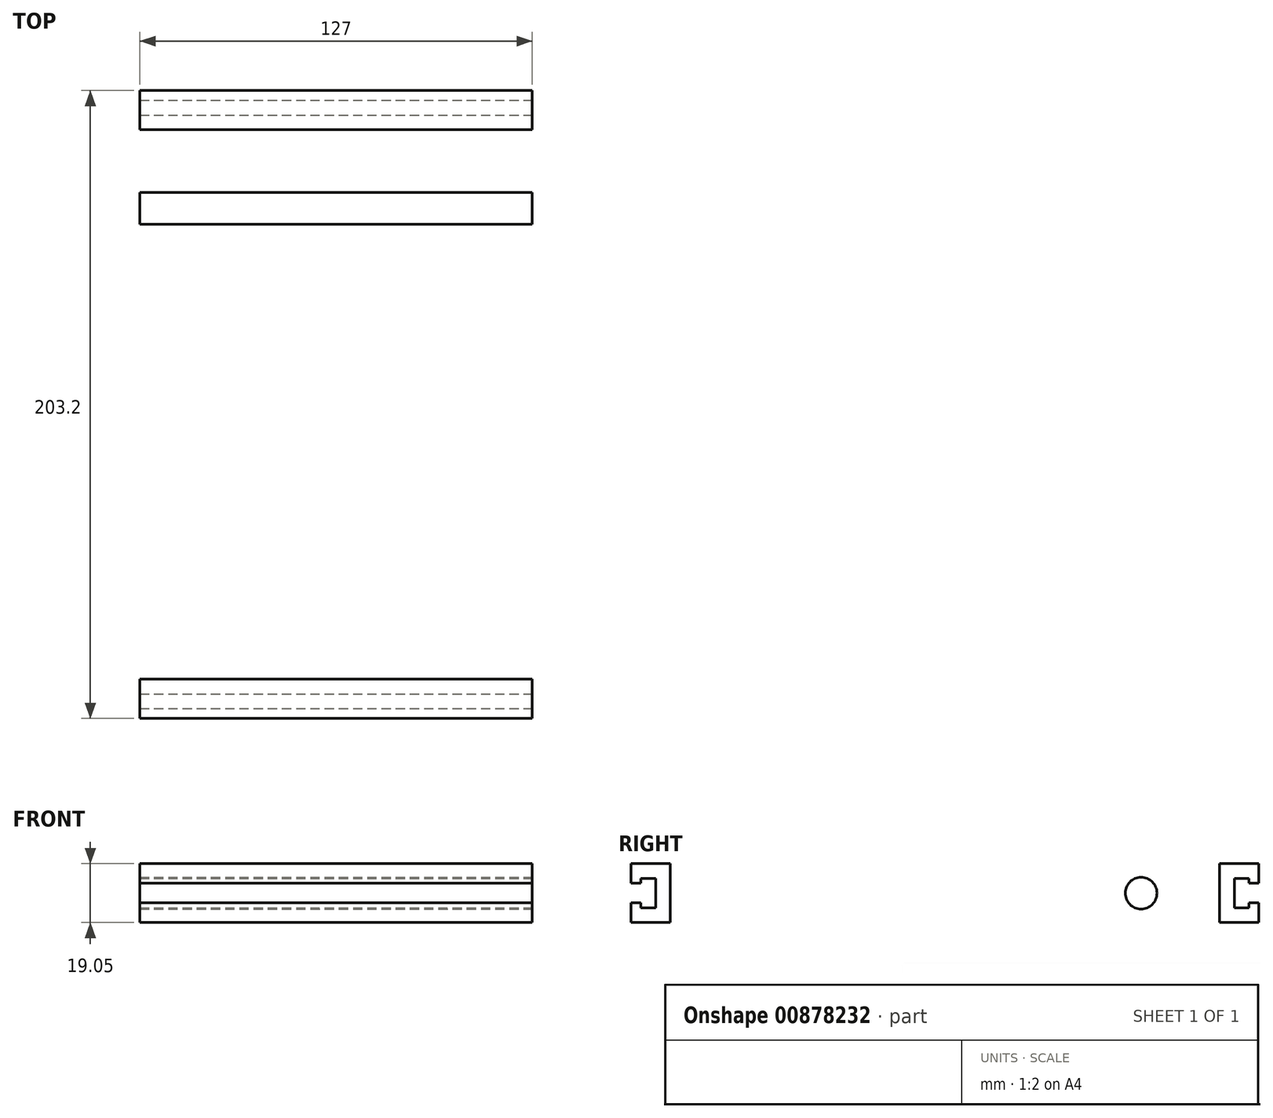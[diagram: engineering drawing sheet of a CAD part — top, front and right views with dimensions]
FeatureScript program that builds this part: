
annotation { "Feature Type Name" : "Feature", "Feature Type Description" : "" }
export const myFeature = defineFeature(function(context is Context, id is Id, definition is map)
    precondition{}
    {
        {
            var Q0;
            Q0=qCreatedBy(makeId("Top.planeOp"),FACE);
            var sketch = newSketch(context, id + "F0", { "sketchPlane" : qUnion([Q0])});
            skLineSegment(sketch, "E0.bottom", {"start": v(0, 0) * mm, "end": v(127, 0) * mm});
            skLineSegment(sketch, "E0.top", {"start": v(0, 177.8) * mm, "end": v(127, 177.8) * mm});
            skLineSegment(sketch, "E0.left", {"start": v(0, 0) * mm, "end": v(0, 177.8) * mm});
            skLineSegment(sketch, "E0.right", {"start": v(127, 0) * mm, "end": v(127, 177.8) * mm});
            skLineSegment(sketch, "E1", {"start": v(0, 88.9) * mm, "end": v(127, 88.9) * mm, "construction": true});
            skSolve(sketch);
        }
        {
            var Q0;
            Q0 = qSketchRegion(id + "F0", true);
            extrude(context, id + "F1", {"entities" : qUnion([Q0]), "depth" : 19.05 * mm, "offsetDistance" : 25.4 * mm});
        }
        {
            var Q0;
            Q0=makeQuery(id+"F1.opExtrude","SWEPT_FACE",FACE,{"disambiguationData":[OSD([sQuery(id+"F0.wireOp",EDGE,"E0.right")])]});
            var sketch = newSketch(context, id + "F2", { "sketchPlane" : qUnion([Q0])});
            skLineSegment(sketch, "E2.bottom", {"start": v(38.1, 19.05) * mm, "end": v(44.45, 19.05) * mm});
            skLineSegment(sketch, "E2.top", {"start": v(38.1, 12.7) * mm, "end": v(44.45, 12.7) * mm});
            skLineSegment(sketch, "E2.left", {"start": v(38.1, 19.05) * mm, "end": v(38.1, 12.7) * mm});
            skLineSegment(sketch, "E2.right", {"start": v(44.45, 19.05) * mm, "end": v(44.45, 12.7) * mm});
            skLineSegment(sketch, "E3.bottom", {"start": v(84.14, 19.05) * mm, "end": v(93.66, 19.05) * mm});
            skLineSegment(sketch, "E3.top", {"start": v(84.14, 12.7) * mm, "end": v(93.66, 12.7) * mm});
            skLineSegment(sketch, "E3.left", {"start": v(84.14, 19.05) * mm, "end": v(84.14, 12.7) * mm});
            skLineSegment(sketch, "E3.right", {"start": v(93.66, 19.05) * mm, "end": v(93.66, 12.7) * mm});
            skLineSegment(sketch, "E4.bottom", {"start": v(80.96, 12.7) * mm, "end": v(96.84, 12.7) * mm});
            skLineSegment(sketch, "E4.top", {"start": v(80.96, 6.35) * mm, "end": v(96.84, 6.35) * mm});
            skLineSegment(sketch, "E4.left", {"start": v(80.96, 12.7) * mm, "end": v(80.96, 6.35) * mm});
            skLineSegment(sketch, "E4.right", {"start": v(96.84, 12.7) * mm, "end": v(96.84, 6.35) * mm});
            skLineSegment(sketch, "E5", {"start": v(88.9, 19.05) * mm, "end": v(88.9, 6.35) * mm, "construction": true});
            skCircle(sketch, "E6", {"center": v(25.4, 9.53) * mm, "radius": 5.13 * mm});
            skLineSegment(sketch, "E7.MirrorCS", {"start": v(133.35, 19.05) * mm, "end": v(133.35, 12.7) * mm});
            skLineSegment(sketch, "E8.MirrorCS", {"start": v(139.7, 19.05) * mm, "end": v(139.7, 12.7) * mm});
            skLineSegment(sketch, "E9.MirrorCS", {"start": v(139.7, 19.05) * mm, "end": v(133.35, 19.05) * mm});
            skLineSegment(sketch, "E10.MirrorCS", {"start": v(139.7, 12.7) * mm, "end": v(133.35, 12.7) * mm});
            skCircle(sketch, "E11.MirrorC", {"center": v(152.4, 9.53) * mm, "radius": 5.13 * mm});
            skLineSegment(sketch, "E12", {"start": v(88.9, 19.05) * mm, "end": v(88.9, 0) * mm, "construction": true});
            skSolve(sketch);
        }
        {
            var Q0;
            Q0=makeQuery(id+"F2.imprint","IMPRINT",FACE,{"disambiguationData":[TD([[makeQuery(id+"F2.imprint","IMPRINT",EDGE,{"derivedFrom":sQuery(id+"F2.wireOp",EDGE,"E2.bottom")}),-1.0]])]});
            var Q1;
            Q1=makeQuery(id+"F2.imprint","IMPRINT",FACE,{"disambiguationData":[TD([[makeQuery(id+"F2.imprint","IMPRINT",EDGE,{"derivedFrom":sQuery(id+"F2.wireOp",EDGE,"8MJqfb7B-8J9h-P5dN-rijc-Vm4WTMmTbfln.bottom")}),-1.0]])]});
            var Q2;
            Q2=makeQuery(id+"F2.imprint","IMPRINT",FACE,{"disambiguationData":[TD([[makeQuery(id+"F2.imprint","IMPRINT",EDGE,{"derivedFrom":sQuery(id+"F2.wireOp",EDGE,"E3.bottom")}),-1.0]])]});
            var Q3;
            Q3=makeQuery(id+"F2.imprint","IMPRINT",FACE,{"disambiguationData":[TD([[makeQuery(id+"F2.imprint","IMPRINT",EDGE,{"derivedFrom":sQuery(id+"F2.wireOp",EDGE,"E4.top")}),1.0]])]});
            var Q4;
            Q4=makeQuery(id+"F2.imprint","IMPRINT",FACE,{"disambiguationData":[TD([[makeQuery(id+"F2.imprint","IMPRINT",EDGE,{"derivedFrom":sQuery(id+"F2.wireOp",EDGE,"E6")}),1.0]])]});
            var Q5;
            Q5=makeQuery(id+"F2.imprint","IMPRINT",FACE,{"disambiguationData":[TD([[makeQuery(id+"F2.imprint","IMPRINT",EDGE,{"derivedFrom":sQuery(id+"F2.wireOp",EDGE,"E11.MirrorC")}),-1.0]])]});
            var Q6;
            Q6=makeQuery(id+"F2.imprint","IMPRINT",FACE,{"disambiguationData":[TD([[makeQuery(id+"F2.imprint","IMPRINT",EDGE,{"derivedFrom":sQuery(id+"F2.wireOp",EDGE,"E7.MirrorCS")}),1.0]])]});
            extrude(context, id + "F3", {"entities" : qUnion([Q0, Q1, Q2, Q3, Q4, Q5, Q6]), "operationType" : NewBodyOperationType.REMOVE, "endBound" : BoundingType.THROUGH_ALL, "oppositeDirection" : true, "depth" : 25.4 * mm, "offsetDistance" : 25.4 * mm});
        }
        {
            var Q0;
            Q0=makeQuery(id+"F1.opExtrude","SWEPT_FACE",FACE,{"disambiguationData":[OSD([sQuery(id+"F0.wireOp",EDGE,"E0.right")])]});
            var sketch = newSketch(context, id + "F4", { "sketchPlane" : qUnion([Q0])});
            skLineSegment(sketch, "E13.bottom", {"start": v(0, 19.05) * mm, "end": v(-12.7, 19.05) * mm});
            skLineSegment(sketch, "E13.top", {"start": v(0, 0) * mm, "end": v(-12.7, 0) * mm});
            skLineSegment(sketch, "E13.left", {"start": v(0, 19.05) * mm, "end": v(0, 0) * mm});
            skLineSegment(sketch, "E13.right", {"start": v(-12.7, 19.05) * mm, "end": v(-12.7, 0) * mm});
            skLineSegment(sketch, "E14.bottom", {"start": v(-12.7, 6.35) * mm, "end": v(-9.52, 6.35) * mm});
            skLineSegment(sketch, "E14.top", {"start": v(-12.7, 12.7) * mm, "end": v(-9.52, 12.7) * mm});
            skLineSegment(sketch, "E14.left", {"start": v(-12.7, 6.35) * mm, "end": v(-12.7, 12.7) * mm});
            skLineSegment(sketch, "E14.right", {"start": v(-9.52, 6.35) * mm, "end": v(-9.52, 12.7) * mm});
            skLineSegment(sketch, "E15.bottom", {"start": v(-9.52, 4.76) * mm, "end": v(-4.76, 4.76) * mm});
            skLineSegment(sketch, "E15.top", {"start": v(-9.52, 14.29) * mm, "end": v(-4.76, 14.29) * mm});
            skLineSegment(sketch, "E15.left", {"start": v(-9.52, 4.76) * mm, "end": v(-9.52, 14.29) * mm});
            skLineSegment(sketch, "E15.right", {"start": v(-4.76, 4.76) * mm, "end": v(-4.76, 14.29) * mm});
            skLineSegment(sketch, "E16", {"start": v(-12.7, 9.53) * mm, "end": v(0, 9.53) * mm, "construction": true});
            skLineSegment(sketch, "E17.MirrorCS", {"start": v(187.32, 6.35) * mm, "end": v(187.32, 12.7) * mm});
            skLineSegment(sketch, "E18.MirrorCS", {"start": v(187.32, 4.76) * mm, "end": v(187.32, 14.29) * mm});
            skLineSegment(sketch, "E19.MirrorCS", {"start": v(177.8, 0) * mm, "end": v(190.5, 0) * mm});
            skLineSegment(sketch, "E20.MirrorCS", {"start": v(187.32, 14.29) * mm, "end": v(182.56, 14.29) * mm});
            skLineSegment(sketch, "E21.MirrorCS", {"start": v(187.32, 4.76) * mm, "end": v(182.56, 4.76) * mm});
            skLineSegment(sketch, "E22.MirrorCS", {"start": v(190.5, 19.05) * mm, "end": v(190.5, 0) * mm});
            skLineSegment(sketch, "E23.MirrorCS", {"start": v(190.5, 6.35) * mm, "end": v(190.5, 12.7) * mm});
            skLineSegment(sketch, "E24.MirrorCS", {"start": v(182.56, 4.76) * mm, "end": v(182.56, 14.29) * mm});
            skLineSegment(sketch, "E25.MirrorCS", {"start": v(177.8, 19.05) * mm, "end": v(190.5, 19.05) * mm});
            skLineSegment(sketch, "E26.MirrorCS", {"start": v(190.5, 9.53) * mm, "end": v(177.8, 9.53) * mm, "construction": true});
            skLineSegment(sketch, "E27.MirrorCS", {"start": v(190.5, 12.7) * mm, "end": v(187.32, 12.7) * mm});
            skLineSegment(sketch, "E28.MirrorCS", {"start": v(190.5, 6.35) * mm, "end": v(187.32, 6.35) * mm});
            skLineSegment(sketch, "E29.MirrorCS", {"start": v(177.8, 19.05) * mm, "end": v(177.8, 0) * mm});
            skSolve(sketch);
        }
        {
            var Q0;
            {var subQ8=sQuery(id+"F4.wireOp",EDGE,"E13.bottom");Q0=makeQuery(id+"F4.imprint","IMPRINT",FACE,{"disambiguationData":[TD([[makeQuery(id+"F4.imprint","IMPRINT",EDGE,{"derivedFrom":subQ8}),1.0]])]});}
            var Q1;
            {var subQ2=sQuery(id+"F4.wireOp",EDGE,"E19.MirrorCS");Q1=makeQuery(id+"F4.imprint","IMPRINT",FACE,{"disambiguationData":[TD([[makeQuery(id+"F4.imprint","IMPRINT",EDGE,{"derivedFrom":subQ2}),1.0]])]});}
            var Q2;
            Q2=qCreatedBy(makeId("Origin.pointOp"),VERTEX);
            extrude(context, id + "F5", {"entities" : qUnion([Q0, Q1]), "endBound" : BoundingType.UP_TO_VERTEX, "oppositeDirection" : true, "depth" : 25.4 * mm, "endBoundEntityVertex" : qUnion([Q2]), "offsetDistance" : 25.4 * mm});
        }
    });
